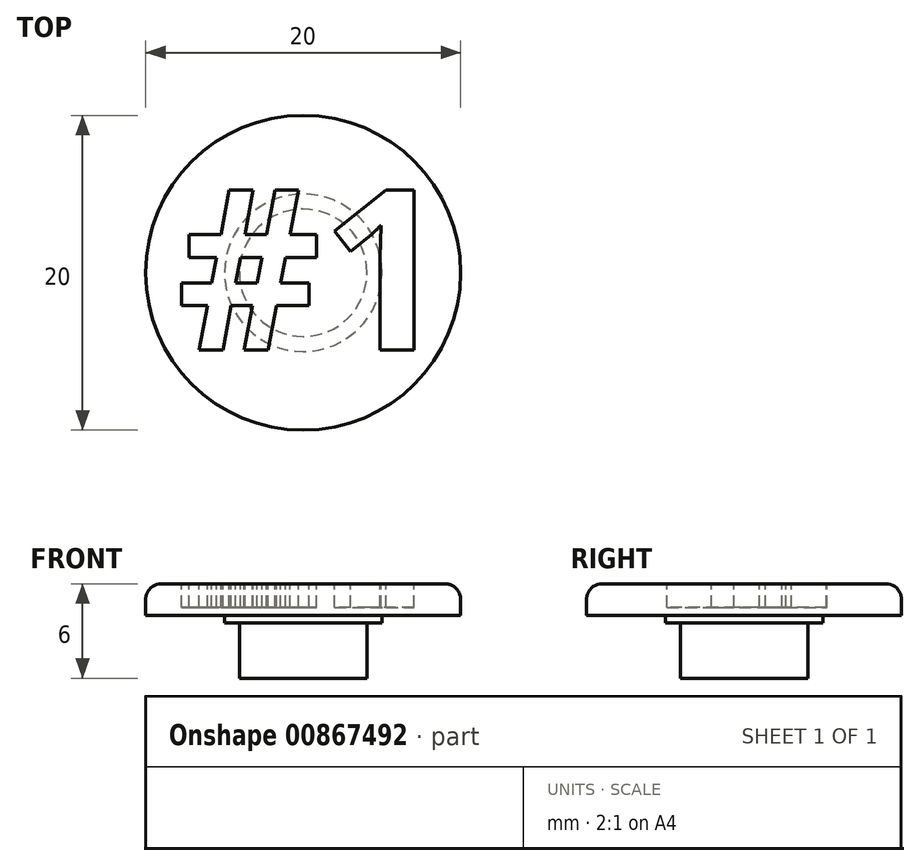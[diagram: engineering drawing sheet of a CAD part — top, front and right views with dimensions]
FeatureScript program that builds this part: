
annotation { "Feature Type Name" : "Feature", "Feature Type Description" : "" }
export const myFeature = defineFeature(function(context is Context, id is Id, definition is map)
    precondition{}
    {
        {
            var Q0;
            Q0=qCreatedBy(makeId("Top.planeOp"),FACE);
            var sketch = newSketch(context, id + "F0", { "sketchPlane" : qUnion([Q0])});
            skCircle(sketch, "E0", {"center": v(0, 0) * mm, "radius": 10 * mm});
            skCircle(sketch, "E1", {"center": v(0, 0) * mm, "radius": 4.05 * mm});
            skCircle(sketch, "E2", {"center": v(0, 0) * mm, "radius": 5 * mm});
            skSolve(sketch);
        }
        {
            var Q0;
            Q0=makeQuery(id+"F0.imprint","IMPRINT",FACE,{"disambiguationData":[TD([[makeQuery(id+"F0.imprint","IMPRINT",EDGE,{"derivedFrom":sQuery(id+"F0.wireOp",EDGE,"E1")}),1.0]])]});
            extrude(context, id + "F1", {"entities" : qUnion([Q0]), "oppositeDirection" : true, "depth" : 6 * mm, "offsetDistance" : 25 * mm});
        }
        {
            var Q0;
            Q0=makeQuery(id+"F0.imprint","IMPRINT",FACE,{"disambiguationData":[TD([[makeQuery(id+"F0.imprint","IMPRINT",EDGE,{"derivedFrom":sQuery(id+"F0.wireOp",EDGE,"E1")}),-1.0]])]});
            extrude(context, id + "F2", {"entities" : qUnion([Q0]), "operationType" : NewBodyOperationType.ADD, "oppositeDirection" : true, "depth" : 2.5 * mm, "offsetDistance" : 25 * mm});
        }
        {
            var Q0;
            Q0=makeQuery(id+"F0.imprint","IMPRINT",FACE,{"disambiguationData":[TD([[makeQuery(id+"F0.imprint","IMPRINT",EDGE,{"derivedFrom":sQuery(id+"F0.wireOp",EDGE,"E0")}),1.0]])]});
            extrude(context, id + "F3", {"entities" : qUnion([Q0]), "operationType" : NewBodyOperationType.ADD, "oppositeDirection" : true, "depth" : 2 * mm, "offsetDistance" : 25 * mm});
        }
        {
            var Q0;
            Q0=makeQuery(id+"F3.opExtrude","CAP_EDGE",EDGE,{"disambiguationData":[OSD([sQuery(id+"F0.wireOp",EDGE,"E0")])],"isStart":true});
            fillet(context, id + "F4", {"entities" : qUnion([Q0]), "radius" : 1 * mm, "tangentPropagation" : true, "allowEdgeOverflow" : false});
        }
        {
            var Q0;
            Q0=qCreatedBy(makeId("Top.planeOp"),FACE);
            var sketch = newSketch(context, id + "F5", { "sketchPlane" : qUnion([Q0])});
            skText(sketch, "E3", { "text": "#1", "fontName": "OpenSans-Bold.ttf"});
            const initialGuessF5  = {"E3": [-0.00805, -0.0049, 1, 0, 0.01025]};
            skSetInitialGuess(sketch, initialGuessF5);
            skSolve(sketch);
        }
        {
            var Q0;
            Q0=qSketchRegion(id+"F5",true);
            extrude(context, id + "F6", {"entities" : qUnion([Q0]), "operationType" : NewBodyOperationType.REMOVE, "oppositeDirection" : true, "depth" : 1.5 * mm, "offsetDistance" : 25 * mm});
        }
    });
